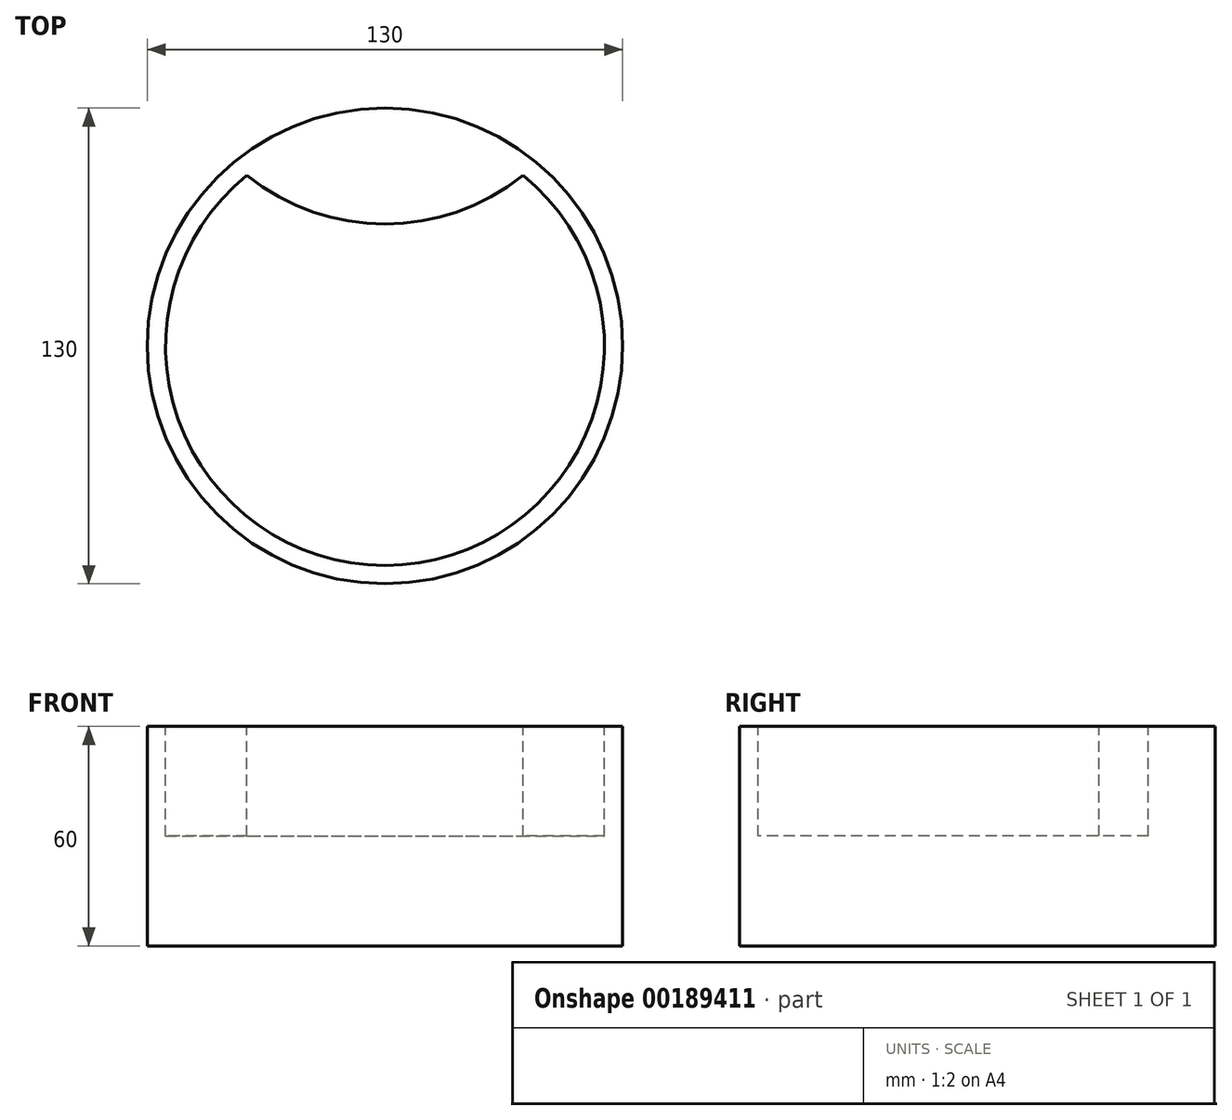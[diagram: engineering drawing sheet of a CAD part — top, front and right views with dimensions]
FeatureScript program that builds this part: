
annotation { "Feature Type Name" : "Feature", "Feature Type Description" : "" }
export const myFeature = defineFeature(function(context is Context, id is Id, definition is map)
    precondition{}
    {
        {
            var Q0;
            Q0=qCreatedBy(makeId("Top.planeOp"),FACE);
            var sketch = newSketch(context, id + "F0", { "sketchPlane" : qUnion([Q0])});
            skCircle(sketch, "E0", {"center": v(0, 0) * mm, "radius": 65 * mm});
            skSolve(sketch);
        }
        {
            var Q0;
            Q0=makeQuery(id+"F0.imprint","IMPRINT",FACE,{"disambiguationData":[TD([[makeQuery(id+"F0.imprint","IMPRINT",EDGE,{"derivedFrom":sQuery(id+"F0.wireOp",EDGE,"E0")}),1.0]])]});
            extrude(context, id + "F1", {"entities" : qUnion([Q0]), "depth" : 60 * mm});
        }
        {
            var Q0;
            Q0=makeQuery(id+"F1.opExtrude","CAP_FACE",FACE,{"disambiguationData":[OSD([sQuery(id+"F0.wireOp",EDGE,"E0")])],"isStart":false});
            var sketch = newSketch(context, id + "F2", { "sketchPlane" : qUnion([Q0])});
            skArc(sketch, "E1", {"start": v(-37.73, 46.65) * mm, "mid": v(0, 33.3) * mm, "end": v(37.73, 46.65) * mm});
            skArc(sketch, "E2", {"start": v(-37.73, 46.65) * mm, "mid": v(0, -60) * mm, "end": v(37.73, 46.65) * mm});
            skLineSegment(sketch, "E3", {"start": v(-41.53, 50) * mm, "end": v(41.53, 50) * mm, "construction": true});
            skSolve(sketch);
        }
        {
            var Q0;
            Q0=makeQuery(id+"F2.imprint","IMPRINT",FACE,{"disambiguationData":[TD([[makeQuery(id+"F2.imprint","IMPRINT",EDGE,{"derivedFrom":sQuery(id+"F2.wireOp",EDGE,"E1")}),-1.0]])]});
            extrude(context, id + "F3", {"entities" : qUnion([Q0]), "operationType" : NewBodyOperationType.REMOVE, "oppositeDirection" : true, "depth" : 30 * mm});
        }
    });
